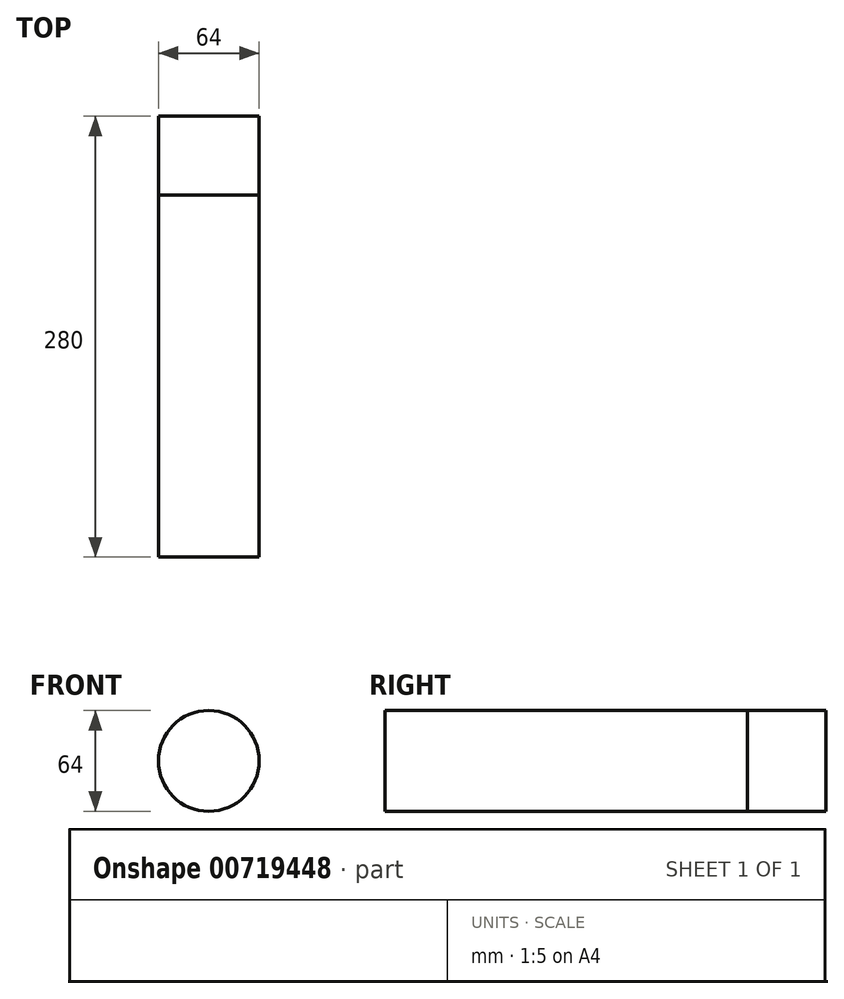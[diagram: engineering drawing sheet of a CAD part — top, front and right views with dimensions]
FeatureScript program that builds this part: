
annotation { "Feature Type Name" : "Feature", "Feature Type Description" : "" }
export const myFeature = defineFeature(function(context is Context, id is Id, definition is map)
    precondition{}
    {
        {
            var Q0;
            Q0=qCreatedBy(makeId("Front.planeOp"),FACE);
            var sketch = newSketch(context, id + "F0", { "sketchPlane" : qUnion([Q0])});
            skCircle(sketch, "E0", {"center": v(0, 0) * mm, "radius": 32 * mm});
            skSolve(sketch);
        }
        {
            var Q0;
            Q0=makeQuery(id+"F0.imprint","IMPRINT",FACE,{"disambiguationData":[TD([[makeQuery(id+"F0.imprint","IMPRINT",EDGE,{"derivedFrom":sQuery(id+"F0.wireOp",EDGE,"E0")}),1.0]])]});
            extrude(context, id + "F1", {"entities" : qUnion([Q0]), "oppositeDirection" : true, "depth" : 230 * mm, "offsetDistance" : 25 * mm});
        }
        {
            var Q0;
            Q0=makeQuery(id+"F1.opExtrude","CAP_FACE",FACE,{"disambiguationData":[OSD([sQuery(id+"F0.wireOp",EDGE,"E0")])],"isStart":false});
            var sketch = newSketch(context, id + "F2", { "sketchPlane" : qUnion([Q0])});
            skCircle(sketch, "E1", {"center": v(0, 0) * mm, "radius": 32 * mm});
            skSolve(sketch);
        }
        {
            var Q0;
            Q0=makeQuery(id+"F2.imprint","IMPRINT",FACE,{"disambiguationData":[TD([[makeQuery(id+"F2.imprint","IMPRINT",EDGE,{"derivedFrom":sQuery(id+"F2.wireOp",EDGE,"E1")}),1.0]])]});
            var Q1;
            Q1=makeQuery(id+"F2.imprint","IMPRINT",FACE,{"disambiguationData":[TD([[makeQuery(id+"F2.imprint","IMPRINT",EDGE,{"derivedFrom":sQuery(id+"F2.wireOp",EDGE,"E1")}),-1.0]])]});
            extrude(context, id + "F3", {"entities" : qUnion([Q0, Q1]), "depth" : 50 * mm, "offsetDistance" : 25 * mm});
        }
    });
